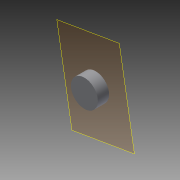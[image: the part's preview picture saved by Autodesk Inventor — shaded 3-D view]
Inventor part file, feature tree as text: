
AUTODESK INVENTOR PART (.ipt)
format: ipt  version: 2014 (Build 180170000, 170)  size: 71,168 bytes
history: native  units: in
note: dims shown in document units (in); Inventor stores cm internally (conversion verified against a paired STEP export)
features: plane x1, extrude x1, sketch x1, reference x1
ambient origin geometry x8: Origin, YZ Plane, XZ Plane, XY Plane, X Axis, Y Axis, Z Axis, Center Point
bodies: Solid1 (feature_tree)
feature tree (4):
  plane  "Work Plane1"
  extrude  "Extrusion1"  [1 undecoded]
  sketch  "Sketch1"  dims[d0=0.0984in d1=0.0in]
  reference  "Reference1"
note: 1 required parameter value undecoded (feature->parameter linkage not recoverable at this tier; creation-order binding heuristic only, values carry confidence <= 0.55)
